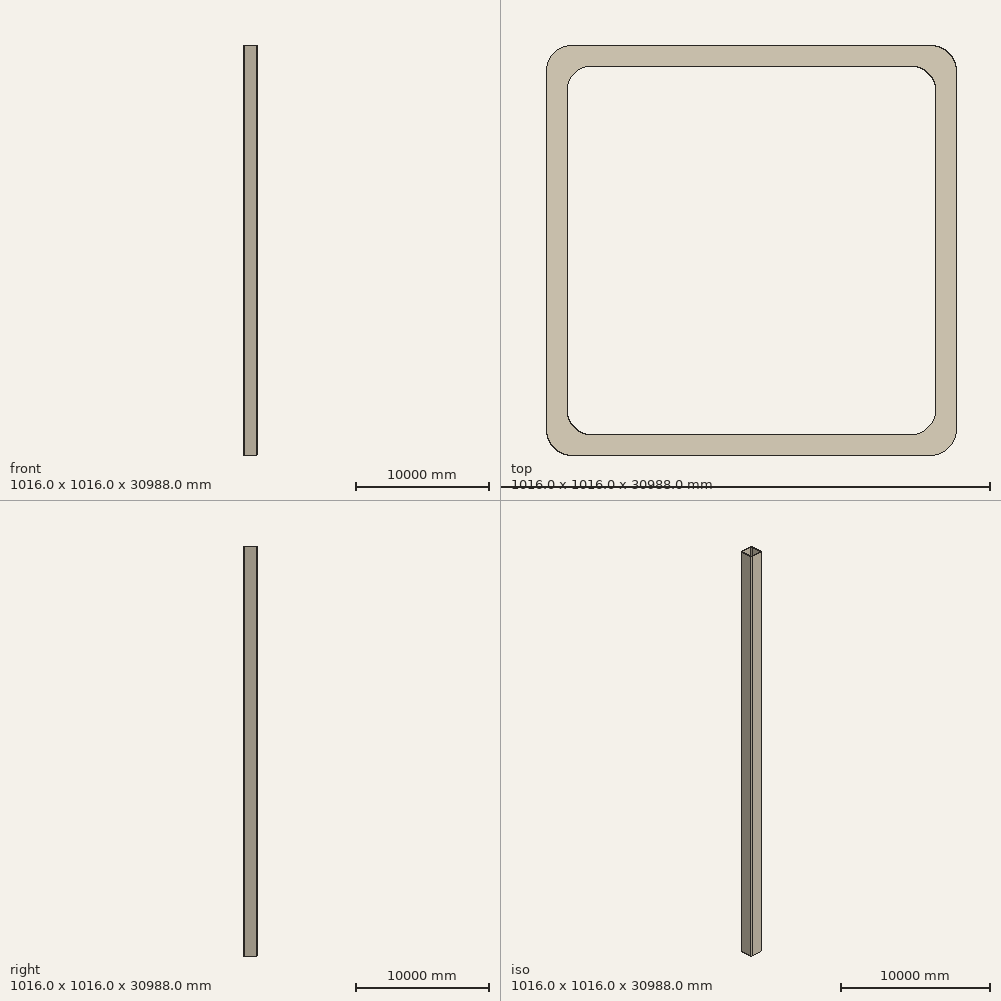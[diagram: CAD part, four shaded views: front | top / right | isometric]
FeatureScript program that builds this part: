
annotation { "Feature Type Name" : "Feature", "Feature Type Description" : "" }
export const myFeature = defineFeature(function(context is Context, id is Id, definition is map)
    precondition{}
    {
        {
            var Q0;
            Q0=qCreatedBy(makeId("Top.planeOp"),FACE);
            var sketch = newSketch(context, id + "F0", { "sketchPlane" : qUnion([Q0])});
            skLineSegment(sketch, "E0.bottom", {"start": v(33.44, 80.64) * mm, "end": v(922.44, 80.64) * mm});
            skLineSegment(sketch, "E0.top", {"start": v(33.44, -935.36) * mm, "end": v(922.44, -935.36) * mm});
            skLineSegment(sketch, "E0.left", {"start": v(-30.06, 17.14) * mm, "end": v(-30.06, -871.86) * mm});
            skLineSegment(sketch, "E0.right", {"start": v(985.94, 17.14) * mm, "end": v(985.94, -871.86) * mm});
            skPoint(sketch, "E1.visualSharp", {"position": v(-30.06, 80.64) * mm});
            skArc(sketch, "E1.filletArc", {"start": v(33.44, 80.64) * mm, "mid": v(-11.46, 62.04) * mm, "end": v(-30.06, 17.14) * mm});
            skPoint(sketch, "E2.visualSharp", {"position": v(985.94, 80.64) * mm});
            skArc(sketch, "E2.filletArc", {"start": v(985.94, 17.14) * mm, "mid": v(967.34, 62.04) * mm, "end": v(922.44, 80.64) * mm});
            skPoint(sketch, "E3.visualSharp", {"position": v(985.94, -935.36) * mm});
            skArc(sketch, "E3.filletArc", {"start": v(922.44, -935.36) * mm, "mid": v(967.34, -916.76) * mm, "end": v(985.94, -871.86) * mm});
            skPoint(sketch, "E4.visualSharp", {"position": v(-30.06, -935.36) * mm});
            skArc(sketch, "E4.filletArc", {"start": v(-30.06, -871.86) * mm, "mid": v(-11.46, -916.76) * mm, "end": v(33.44, -935.36) * mm});
            skLineSegment(sketch, "E5.bottom", {"start": v(84.24, 29.84) * mm, "end": v(871.64, 29.84) * mm});
            skLineSegment(sketch, "E5.top", {"start": v(84.24, -884.56) * mm, "end": v(871.64, -884.56) * mm});
            skLineSegment(sketch, "E5.left", {"start": v(20.74, -33.66) * mm, "end": v(20.74, -821.06) * mm});
            skLineSegment(sketch, "E5.right", {"start": v(935.14, -33.66) * mm, "end": v(935.14, -821.06) * mm});
            skPoint(sketch, "E6.visualSharp", {"position": v(20.74, -884.56) * mm});
            skArc(sketch, "E6.filletArc", {"start": v(20.74, -821.06) * mm, "mid": v(39.34, -865.96) * mm, "end": v(84.24, -884.56) * mm});
            skPoint(sketch, "E7.visualSharp", {"position": v(20.74, 29.84) * mm});
            skArc(sketch, "E7.filletArc", {"start": v(84.24, 29.84) * mm, "mid": v(39.34, 11.24) * mm, "end": v(20.74, -33.66) * mm});
            skPoint(sketch, "E8.visualSharp", {"position": v(935.14, 29.84) * mm});
            skArc(sketch, "E8.filletArc", {"start": v(935.14, -33.66) * mm, "mid": v(916.54, 11.24) * mm, "end": v(871.64, 29.84) * mm});
            skPoint(sketch, "E9.visualSharp", {"position": v(935.14, -884.56) * mm});
            skArc(sketch, "E9.filletArc", {"start": v(871.64, -884.56) * mm, "mid": v(916.54, -865.96) * mm, "end": v(935.14, -821.06) * mm});
            skSolve(sketch);
        }
        {
            var Q0;
            Q0 = qSketchRegion(id + "F0", true);
            extrude(context, id + "F1", {"entities" : qUnion([Q0]), "depth" : 30988 * mm, "offsetDistance" : 25.4 * mm});
        }
    });
